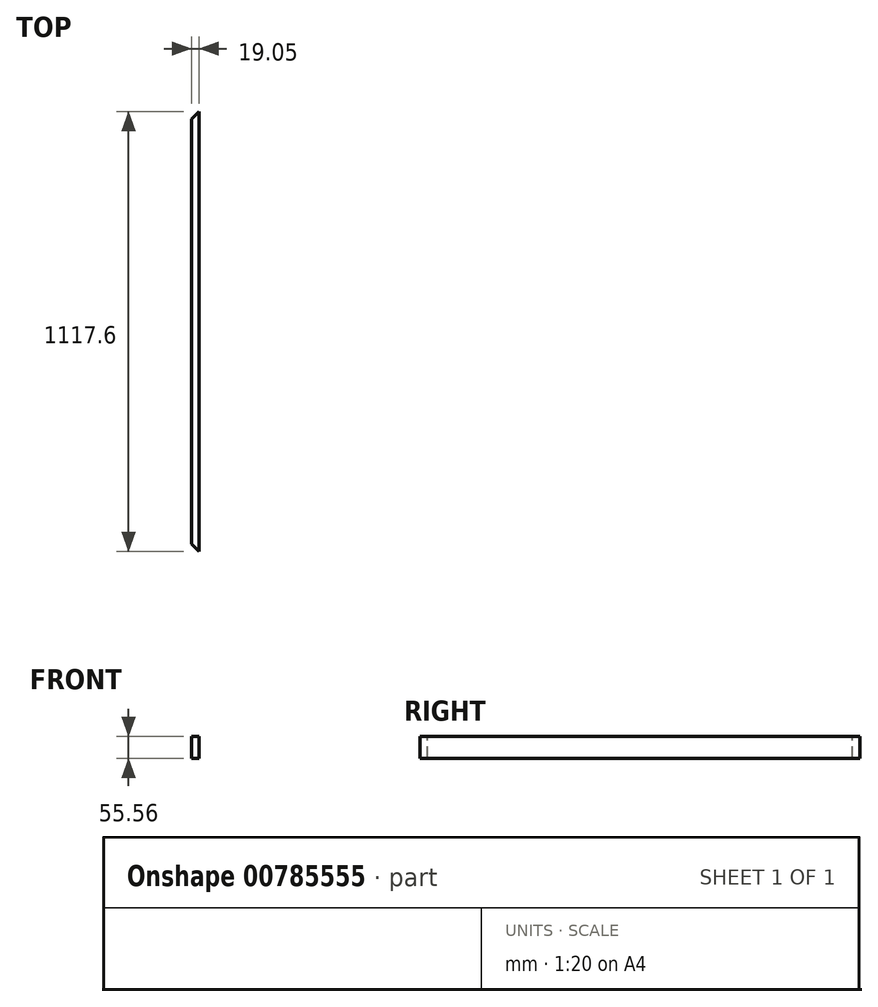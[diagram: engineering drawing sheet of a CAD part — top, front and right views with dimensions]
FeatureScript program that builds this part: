
annotation { "Feature Type Name" : "Feature", "Feature Type Description" : "" }
export const myFeature = defineFeature(function(context is Context, id is Id, definition is map)
    precondition{}
    {
        {
            var Q0;
            Q0=qCreatedBy(makeId("Right.planeOp"),FACE);
            var sketch = newSketch(context, id + "F0", { "sketchPlane" : qUnion([Q0])});
            skLineSegment(sketch, "E0.bottom", {"start": v(558.8, 27.78) * mm, "end": v(-558.8, 27.78) * mm});
            skLineSegment(sketch, "E0.top", {"start": v(558.8, -27.78) * mm, "end": v(-558.8, -27.78) * mm});
            skLineSegment(sketch, "E0.left", {"start": v(558.8, 27.78) * mm, "end": v(558.8, -27.78) * mm});
            skLineSegment(sketch, "E0.right", {"start": v(-558.8, 27.78) * mm, "end": v(-558.8, -27.78) * mm});
            skPoint(sketch, "E0.middle", {"position": v(0, 0) * mm});
            skSolve(sketch);
        }
        {
            var Q0;
            Q0 = qSketchRegion(id + "F0", true);
            extrude(context, id + "F1", {"entities" : qUnion([Q0]), "depth" : 19.05 * mm, "offsetDistance" : 25.4 * mm});
        }
        {
            var Q0;
            Q0=makeQuery(id+"F1.opExtrude","SWEPT_FACE",FACE,{"disambiguationData":[OSD([sQuery(id+"F0.wireOp",EDGE,"E0.bottom")])]});
            var sketch = newSketch(context, id + "F2", { "sketchPlane" : qUnion([Q0])});
            skLineSegment(sketch, "E1", {"start": v(19.05, -558.8) * mm, "end": v(0, -539.75) * mm});
            skLineSegment(sketch, "E2.MirrorCS", {"start": v(19.05, 558.8) * mm, "end": v(0, 539.75) * mm});
            skSolve(sketch);
        }
        {
            var Q0;
            Q0 = qSketchRegion(id + "F2", true);
            var Q1;
            {var subQ0=sQuery(id+"F2.wireOp",EDGE,"E2.MirrorCS");Q1=makeQuery(id+"F2.imprint","IMPRINT",FACE,{"disambiguationData":[TD([[makeQuery(id+"F2.imprint","IMPRINT",EDGE,{"derivedFrom":subQ0}),-1.0]])]});}
            var Q2;
            {var subQ0=sQuery(id+"F2.wireOp",EDGE,"E1");Q2=makeQuery(id+"F2.imprint","IMPRINT",FACE,{"disambiguationData":[TD([[makeQuery(id+"F2.imprint","IMPRINT",EDGE,{"derivedFrom":subQ0}),1.0]])]});}
            extrude(context, id + "F3", {"entities" : qUnion([Q0, Q1, Q2]), "operationType" : NewBodyOperationType.REMOVE, "endBound" : BoundingType.THROUGH_ALL, "oppositeDirection" : true, "depth" : 25.4 * mm, "offsetDistance" : 25.4 * mm});
        }
    });
